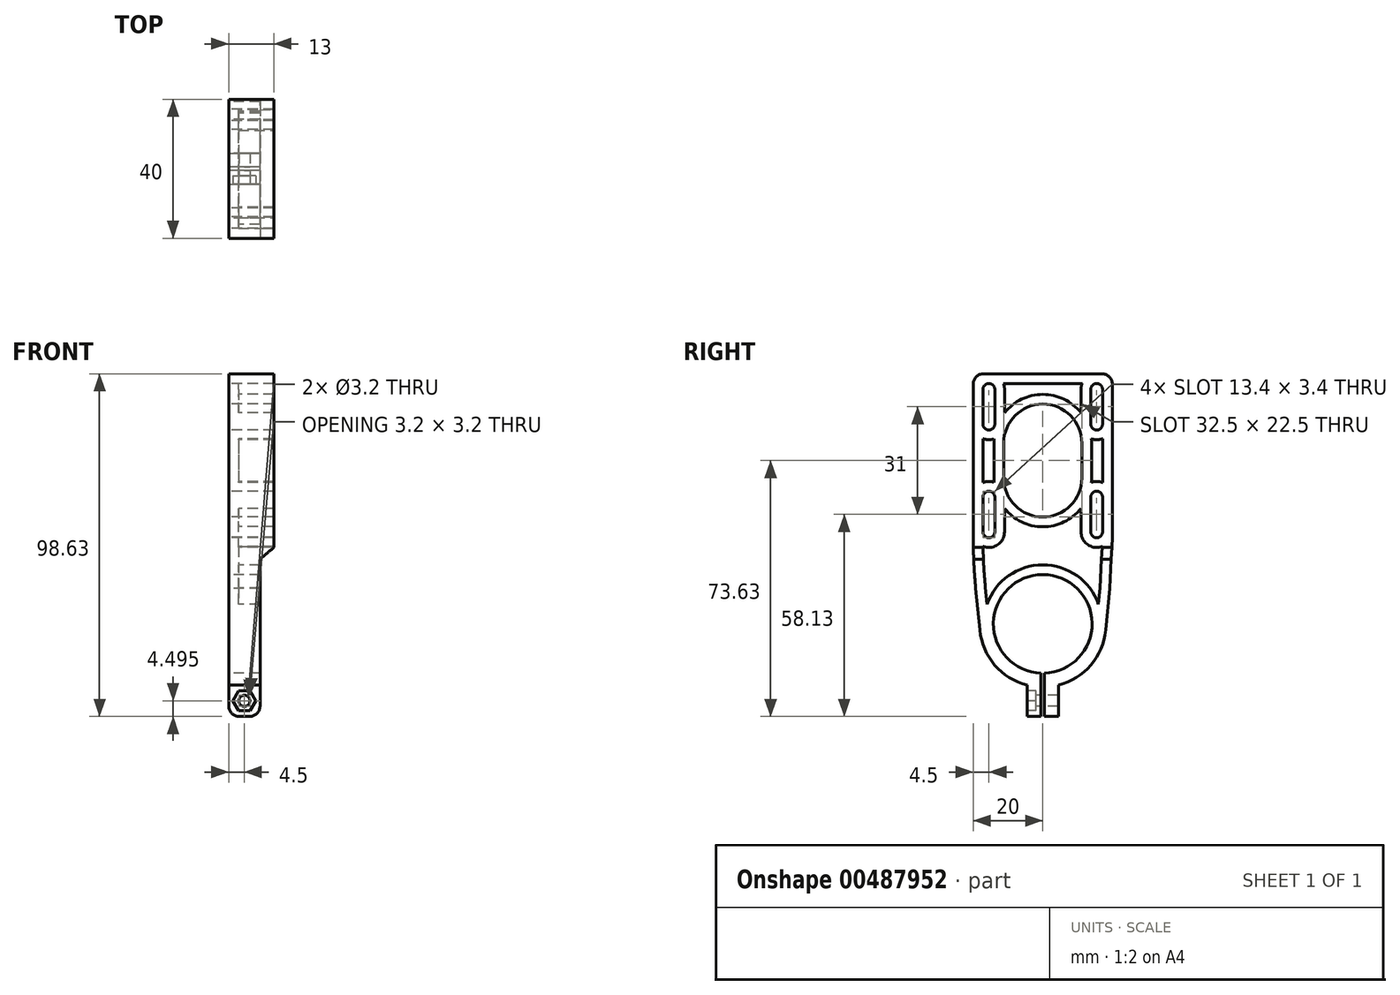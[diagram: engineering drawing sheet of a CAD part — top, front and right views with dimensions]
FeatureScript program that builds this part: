
annotation { "Feature Type Name" : "Feature", "Feature Type Description" : "" }
export const myFeature = defineFeature(function(context is Context, id is Id, definition is map)
    precondition{}
    {
        {
            var Q0;
            Q0=qCreatedBy(makeId("Right.planeOp"),FACE);
            var sketch = newSketch(context, id + "F0", { "sketchPlane" : qUnion([Q0])});
            skLineSegment(sketch, "E0", {"start": v(-20, 69) * mm, "end": v(-20, 25) * mm});
            skLineSegment(sketch, "E1", {"start": v(-19.28, 10.18) * mm, "end": v(-18.11, -1.77) * mm});
            skLineSegment(sketch, "E2", {"start": v(-0.5, -14.2) * mm, "end": v(-0.5, -26.63) * mm});
            skLineSegment(sketch, "E3", {"start": v(-0.5, -26.63) * mm, "end": v(-4.5, -26.63) * mm});
            skLineSegment(sketch, "E4", {"start": v(-4.5, -26.63) * mm, "end": v(-4.5, -17.63) * mm});
            skLineSegment(sketch, "E5", {"start": v(-17, 72) * mm, "end": v(0, 72) * mm});
            skArc(sketch, "E6", {"start": v(-0.5, -14.2) * mm, "mid": v(-14.2, 0.25) * mm, "end": v(0, 14.2) * mm});
            skArc(sketch, "E7", {"start": v(-4.5, -17.63) * mm, "mid": v(-13.81, -11.85) * mm, "end": v(-18.11, -1.77) * mm});
            skLineSegment(sketch, "E8.left", {"start": v(-17.2, 67.5) * mm, "end": v(-17.2, 57.5) * mm});
            skLineSegment(sketch, "E8.right", {"start": v(-13.8, 67.5) * mm, "end": v(-13.8, 57.5) * mm});
            skArc(sketch, "E9", {"start": v(0, 63.25) * mm, "mid": v(-7.95, 59.95) * mm, "end": v(-11.25, 52) * mm});
            skLineSegment(sketch, "E10", {"start": v(-11.25, 52) * mm, "end": v(-11.25, 42) * mm});
            skArc(sketch, "E11", {"start": v(-11.25, 42) * mm, "mid": v(-7.95, 34.05) * mm, "end": v(0, 30.75) * mm});
            skArc(sketch, "E12", {"start": v(-17.2, 67.5) * mm, "mid": v(-15.5, 69.2) * mm, "end": v(-13.8, 67.5) * mm});
            skArc(sketch, "E13", {"start": v(-17.2, 57.5) * mm, "mid": v(-15.5, 55.8) * mm, "end": v(-13.8, 57.5) * mm});
            skPoint(sketch, "E14.visualSharp", {"position": v(-20, 72) * mm});
            skArc(sketch, "E14.filletArc", {"start": v(-17, 72) * mm, "mid": v(-19.12, 71.12) * mm, "end": v(-20, 69) * mm});
            skLineSegment(sketch, "E15", {"start": v(-20, 47) * mm, "end": v(0, 47) * mm, "construction": true});
            skArc(sketch, "E16.MirrorCS", {"start": v(-17.2, 36.5) * mm, "mid": v(-15.5, 38.2) * mm, "end": v(-13.8, 36.5) * mm});
            skLineSegment(sketch, "E17.MirrorCS", {"start": v(-13.8, 26.5) * mm, "end": v(-13.8, 36.5) * mm});
            skArc(sketch, "E18.MirrorCS", {"start": v(-17.2, 26.5) * mm, "mid": v(-15.5, 24.8) * mm, "end": v(-13.8, 26.5) * mm});
            skLineSegment(sketch, "E19.MirrorCS", {"start": v(-17.2, 26.5) * mm, "end": v(-17.2, 36.5) * mm});
            skArc(sketch, "E20.MirrorCS", {"start": v(0, 63.25) * mm, "mid": v(7.95, 59.95) * mm, "end": v(11.25, 52) * mm});
            skLineSegment(sketch, "E21.MirrorCS", {"start": v(11.25, 52) * mm, "end": v(11.25, 42) * mm});
            skArc(sketch, "E22.MirrorCS", {"start": v(11.25, 42) * mm, "mid": v(7.95, 34.05) * mm, "end": v(0, 30.75) * mm});
            skArc(sketch, "E23.MirrorCS", {"start": v(17.2, 57.5) * mm, "mid": v(15.5, 55.8) * mm, "end": v(13.8, 57.5) * mm});
            skLineSegment(sketch, "E24.MirrorCS", {"start": v(13.8, 67.5) * mm, "end": v(13.8, 57.5) * mm});
            skLineSegment(sketch, "E25.MirrorCS", {"start": v(17.2, 67.5) * mm, "end": v(17.2, 57.5) * mm});
            skArc(sketch, "E26.MirrorCS", {"start": v(17.2, 67.5) * mm, "mid": v(15.5, 69.2) * mm, "end": v(13.8, 67.5) * mm});
            skLineSegment(sketch, "E27.MirrorCS", {"start": v(17, 72) * mm, "end": v(0, 72) * mm});
            skArc(sketch, "E28.MirrorCS", {"start": v(17, 72) * mm, "mid": v(19.12, 71.12) * mm, "end": v(20, 69) * mm});
            skLineSegment(sketch, "E29.MirrorCS", {"start": v(20, 69) * mm, "end": v(20, 25) * mm});
            skLineSegment(sketch, "E30.MirrorCS", {"start": v(20, 25) * mm, "end": v(19.28, 10.18) * mm});
            skLineSegment(sketch, "E31.MirrorCS", {"start": v(19.28, 10.18) * mm, "end": v(18.11, -1.77) * mm});
            skArc(sketch, "E32.MirrorCS", {"start": v(4.5, -17.63) * mm, "mid": v(13.81, -11.85) * mm, "end": v(18.11, -1.77) * mm});
            skArc(sketch, "E33.MirrorCS", {"start": v(0.5, -14.2) * mm, "mid": v(14.2, 0.25) * mm, "end": v(0, 14.2) * mm});
            skLineSegment(sketch, "E34.MirrorCS", {"start": v(0.5, -14.2) * mm, "end": v(0.5, -26.63) * mm});
            skLineSegment(sketch, "E35.MirrorCS", {"start": v(4.5, -26.63) * mm, "end": v(4.5, -17.63) * mm});
            skLineSegment(sketch, "E36.MirrorCS", {"start": v(0.5, -26.63) * mm, "end": v(4.5, -26.63) * mm});
            skLineSegment(sketch, "E37.MirrorCS", {"start": v(13.8, 26.5) * mm, "end": v(13.8, 36.5) * mm});
            skArc(sketch, "E38.MirrorCS", {"start": v(17.2, 36.5) * mm, "mid": v(15.5, 38.2) * mm, "end": v(13.8, 36.5) * mm});
            skLineSegment(sketch, "E39.MirrorCS", {"start": v(17.2, 26.5) * mm, "end": v(17.2, 36.5) * mm});
            skArc(sketch, "E40.MirrorCS", {"start": v(17.2, 26.5) * mm, "mid": v(15.5, 24.8) * mm, "end": v(13.8, 26.5) * mm});
            skArc(sketch, "E41", {"start": v(-19.28, 10.18) * mm, "mid": v(-19.82, 17.58) * mm, "end": v(-20, 25) * mm});
            skSolve(sketch);
        }
        {
            var Q0;
            Q0=makeQuery(id+"F0.imprint","IMPRINT",FACE,{"disambiguationData":[TD([[makeQuery(id+"F0.imprint","IMPRINT",EDGE,{"derivedFrom":sQuery(id+"F0.wireOp",EDGE,"E0")}),1.0]])]});
            extrude(context, id + "F1", {"entities" : qUnion([Q0]), "depth" : 13 * mm});
        }
        {
            var Q0;
            Q0=makeQuery(id+"F1.opExtrude","SWEPT_FACE",FACE,{"disambiguationData":[OSD([sQuery(id+"F0.wireOp",EDGE,"E4")])]});
            var sketch = newSketch(context, id + "F2", { "sketchPlane" : qUnion([Q0])});
            skPoint(sketch, "E42", {"position": v(4.5, -22.13) * mm});
            skPoint(sketch, "E42.positionSnap0", {"position": v(13, -22.13) * mm});
            skPoint(sketch, "E43", {"position": v(6.5, -26.63) * mm});
            skCircle(sketch, "E44.cCircle", {"center": v(4.5, -22.13) * mm, "radius": 2.85 * mm, "construction": true});
            skLineSegment(sketch, "E44.0", {"start": v(2.85, -19.28) * mm, "end": v(6.15, -19.28) * mm});
            skLineSegment(sketch, "E44.1", {"start": v(6.15, -19.28) * mm, "end": v(7.8, -22.13) * mm});
            skLineSegment(sketch, "E44.2", {"start": v(7.8, -22.13) * mm, "end": v(6.15, -24.98) * mm});
            skLineSegment(sketch, "E44.3", {"start": v(6.15, -24.98) * mm, "end": v(2.85, -24.98) * mm});
            skLineSegment(sketch, "E44.4", {"start": v(2.85, -24.98) * mm, "end": v(1.2, -22.13) * mm});
            skLineSegment(sketch, "E44.5", {"start": v(1.2, -22.13) * mm, "end": v(2.85, -19.28) * mm});
            skPoint(sketch, "E44.0.midPoint", {"position": v(4.5, -19.28) * mm});
            skLineSegment(sketch, "E45", {"start": v(4.5, -22.13) * mm, "end": v(0, -22.13) * mm});
            skLineSegment(sketch, "E46", {"start": v(4.5, -22.13) * mm, "end": v(4.5, -26.63) * mm});
            skPoint(sketch, "E46.endSnap0", {"position": v(4.5, -24.98) * mm});
            skSolve(sketch);
        }
        {
            var Q0;
            Q0=sQuery(id+"F2.wireOp",VERTEX,"E42");
            var Q1;
            Q1=makeQuery(id+"F1.opExtrude","SWEPT_BODY",BODY,{"disambiguationData":[OSD([sQuery(id+"F0.wireOp",EDGE,"E0"),sQuery(id+"F0.wireOp",EDGE,"L069Me0u-pvYU-BFJx-tYy8-LTSNjWhxfS9e"),sQuery(id+"F0.wireOp",EDGE,"E1"),sQuery(id+"F0.wireOp",EDGE,"E2"),sQuery(id+"F0.wireOp",EDGE,"E3"),sQuery(id+"F0.wireOp",EDGE,"E4"),sQuery(id+"F0.wireOp",EDGE,"E5"),sQuery(id+"F0.wireOp",EDGE,"E6"),sQuery(id+"F0.wireOp",EDGE,"E7"),sQuery(id+"F0.wireOp",EDGE,"E8.left"),sQuery(id+"F0.wireOp",EDGE,"E8.right"),sQuery(id+"F0.wireOp",EDGE,"E9"),sQuery(id+"F0.wireOp",EDGE,"E10"),sQuery(id+"F0.wireOp",EDGE,"E11"),sQuery(id+"F0.wireOp",EDGE,"E12"),sQuery(id+"F0.wireOp",EDGE,"E13"),sQuery(id+"F0.wireOp",EDGE,"E14.filletArc"),sQuery(id+"F0.wireOp",EDGE,"E16.MirrorCS"),sQuery(id+"F0.wireOp",EDGE,"E17.MirrorCS"),sQuery(id+"F0.wireOp",EDGE,"E18.MirrorCS"),sQuery(id+"F0.wireOp",EDGE,"E19.MirrorCS"),sQuery(id+"F0.wireOp",EDGE,"E20.MirrorCS"),sQuery(id+"F0.wireOp",EDGE,"E21.MirrorCS"),sQuery(id+"F0.wireOp",EDGE,"E22.MirrorCS"),sQuery(id+"F0.wireOp",EDGE,"E23.MirrorCS"),sQuery(id+"F0.wireOp",EDGE,"E24.MirrorCS"),sQuery(id+"F0.wireOp",EDGE,"E25.MirrorCS"),sQuery(id+"F0.wireOp",EDGE,"E26.MirrorCS"),sQuery(id+"F0.wireOp",EDGE,"E27.MirrorCS"),sQuery(id+"F0.wireOp",EDGE,"E28.MirrorCS"),sQuery(id+"F0.wireOp",EDGE,"E29.MirrorCS"),sQuery(id+"F0.wireOp",EDGE,"E30.MirrorCS"),sQuery(id+"F0.wireOp",EDGE,"E31.MirrorCS"),sQuery(id+"F0.wireOp",EDGE,"E32.MirrorCS"),sQuery(id+"F0.wireOp",EDGE,"E33.MirrorCS"),sQuery(id+"F0.wireOp",EDGE,"E34.MirrorCS"),sQuery(id+"F0.wireOp",EDGE,"E35.MirrorCS"),sQuery(id+"F0.wireOp",EDGE,"E36.MirrorCS"),sQuery(id+"F0.wireOp",EDGE,"E37.MirrorCS"),sQuery(id+"F0.wireOp",EDGE,"E38.MirrorCS"),sQuery(id+"F0.wireOp",EDGE,"E39.MirrorCS"),sQuery(id+"F0.wireOp",EDGE,"E40.MirrorCS")])]});
            hole(context, id + "F3", {"style" : HoleStyle.SIMPLE, "endStyle" : HoleEndStyle.THROUGH, "holeDiameter" : 3.2 * mm, "tappedDepth" : 12 * mm, "tapClearance" : 3, "locations" : qUnion([Q0]), "scope" : qUnion([Q1])});
        }
        {
            var Q0;
            Q0=makeQuery(id+"F1.opExtrude","CAP_FACE",FACE,{"disambiguationData":[OSD([sQuery(id+"F0.wireOp",EDGE,"E0"),sQuery(id+"F0.wireOp",EDGE,"L069Me0u-pvYU-BFJx-tYy8-LTSNjWhxfS9e"),sQuery(id+"F0.wireOp",EDGE,"E1"),sQuery(id+"F0.wireOp",EDGE,"E2"),sQuery(id+"F0.wireOp",EDGE,"E3"),sQuery(id+"F0.wireOp",EDGE,"E4"),sQuery(id+"F0.wireOp",EDGE,"E5"),sQuery(id+"F0.wireOp",EDGE,"E6"),sQuery(id+"F0.wireOp",EDGE,"E7"),sQuery(id+"F0.wireOp",EDGE,"E8.left"),sQuery(id+"F0.wireOp",EDGE,"E8.right"),sQuery(id+"F0.wireOp",EDGE,"E9"),sQuery(id+"F0.wireOp",EDGE,"E10"),sQuery(id+"F0.wireOp",EDGE,"E11"),sQuery(id+"F0.wireOp",EDGE,"E12"),sQuery(id+"F0.wireOp",EDGE,"E13"),sQuery(id+"F0.wireOp",EDGE,"E14.filletArc"),sQuery(id+"F0.wireOp",EDGE,"E16.MirrorCS"),sQuery(id+"F0.wireOp",EDGE,"E17.MirrorCS"),sQuery(id+"F0.wireOp",EDGE,"E18.MirrorCS"),sQuery(id+"F0.wireOp",EDGE,"E19.MirrorCS"),sQuery(id+"F0.wireOp",EDGE,"E20.MirrorCS"),sQuery(id+"F0.wireOp",EDGE,"E21.MirrorCS"),sQuery(id+"F0.wireOp",EDGE,"E22.MirrorCS"),sQuery(id+"F0.wireOp",EDGE,"E23.MirrorCS"),sQuery(id+"F0.wireOp",EDGE,"E24.MirrorCS"),sQuery(id+"F0.wireOp",EDGE,"E25.MirrorCS"),sQuery(id+"F0.wireOp",EDGE,"E26.MirrorCS"),sQuery(id+"F0.wireOp",EDGE,"E27.MirrorCS"),sQuery(id+"F0.wireOp",EDGE,"E28.MirrorCS"),sQuery(id+"F0.wireOp",EDGE,"E29.MirrorCS"),sQuery(id+"F0.wireOp",EDGE,"E30.MirrorCS"),sQuery(id+"F0.wireOp",EDGE,"E31.MirrorCS"),sQuery(id+"F0.wireOp",EDGE,"E32.MirrorCS"),sQuery(id+"F0.wireOp",EDGE,"E33.MirrorCS"),sQuery(id+"F0.wireOp",EDGE,"E34.MirrorCS"),sQuery(id+"F0.wireOp",EDGE,"E35.MirrorCS"),sQuery(id+"F0.wireOp",EDGE,"E36.MirrorCS"),sQuery(id+"F0.wireOp",EDGE,"E37.MirrorCS"),sQuery(id+"F0.wireOp",EDGE,"E38.MirrorCS"),sQuery(id+"F0.wireOp",EDGE,"E39.MirrorCS"),sQuery(id+"F0.wireOp",EDGE,"E40.MirrorCS")])],"isStart":false});
            shell(context, id + "F4", {"entities" : qUnion([Q0]), "thickness" : 2.8 * mm});
        }
        {
            var Q0;
            Q0=makeQuery(id+"F1.opExtrude","SWEPT_FACE",FACE,{"disambiguationData":[OSD([sQuery(id+"F0.wireOp",EDGE,"E0")])]});
            var sketch = newSketch(context, id + "F5", { "sketchPlane" : qUnion([Q0])});
            skLineSegment(sketch, "E47", {"start": v(13, 22) * mm, "end": v(9, 18.64) * mm});
            skLineSegment(sketch, "E48", {"start": v(9, 18.64) * mm, "end": v(9, -28) * mm});
            skLineSegment(sketch, "E49", {"start": v(9, -28) * mm, "end": v(13, -28) * mm});
            skLineSegment(sketch, "E50", {"start": v(13, -28) * mm, "end": v(13, 22) * mm});
            skSolve(sketch);
        }
        {
            var Q0;
            Q0=makeQuery(id+"F5.imprint","IMPRINT",FACE,{"disambiguationData":[TD([[makeQuery(id+"F5.imprint","IMPRINT",EDGE,{"derivedFrom":sQuery(id+"F5.wireOp",EDGE,"E47")}),1.0]])]});
            extrude(context, id + "F6", {"entities" : qUnion([Q0]), "operationType" : NewBodyOperationType.REMOVE, "endBound" : BoundingType.THROUGH_ALL, "oppositeDirection" : true, "depth" : 25 * mm});
        }
        {
            var Q0;
            Q0=qSketchRegion(id+"F2",true);
            extrude(context, id + "F7", {"entities" : qUnion([Q0]), "operationType" : NewBodyOperationType.REMOVE, "oppositeDirection" : true, "depth" : 2.5 * mm});
        }
        {
            var Q0;
            Q0=makeQuery(id+"F1.opExtrude","CAP_EDGE",EDGE,{"disambiguationData":[OSD([sQuery(id+"F0.wireOp",EDGE,"E3")])],"isStart":true});
            var Q1;
            Q1=makeQuery(id+"F1.opExtrude","CAP_EDGE",EDGE,{"disambiguationData":[OSD([sQuery(id+"F0.wireOp",EDGE,"E36.MirrorCS")])],"isStart":true});
            var Q2;
            Q2=makeQuery(id+"F6.boolean.opBoolean","INTERSECT",EDGE,{"derivedFrom":[makeQuery(id+"F1.opExtrude","SWEPT_FACE",FACE,{"disambiguationData":[OSD([sQuery(id+"F0.wireOp",EDGE,"E3")])]}),makeQuery(id+"F6.opExtrude","SWEPT_FACE",FACE,{"disambiguationData":[OSD([sQuery(id+"F5.wireOp",EDGE,"E48")])]})]});
            var Q3;
            Q3=makeQuery(id+"F6.boolean.opBoolean","INTERSECT",EDGE,{"derivedFrom":[makeQuery(id+"F1.opExtrude","SWEPT_FACE",FACE,{"disambiguationData":[OSD([sQuery(id+"F0.wireOp",EDGE,"E36.MirrorCS")])]}),makeQuery(id+"F6.opExtrude","SWEPT_FACE",FACE,{"disambiguationData":[OSD([sQuery(id+"F5.wireOp",EDGE,"E48")])]})]});
            fillet(context, id + "F8", {"entities" : qUnion([Q0, Q1, Q2, Q3]), "radius" : 3 * mm, "tangentPropagation" : true, "allowEdgeOverflow" : false});
        }
    });
